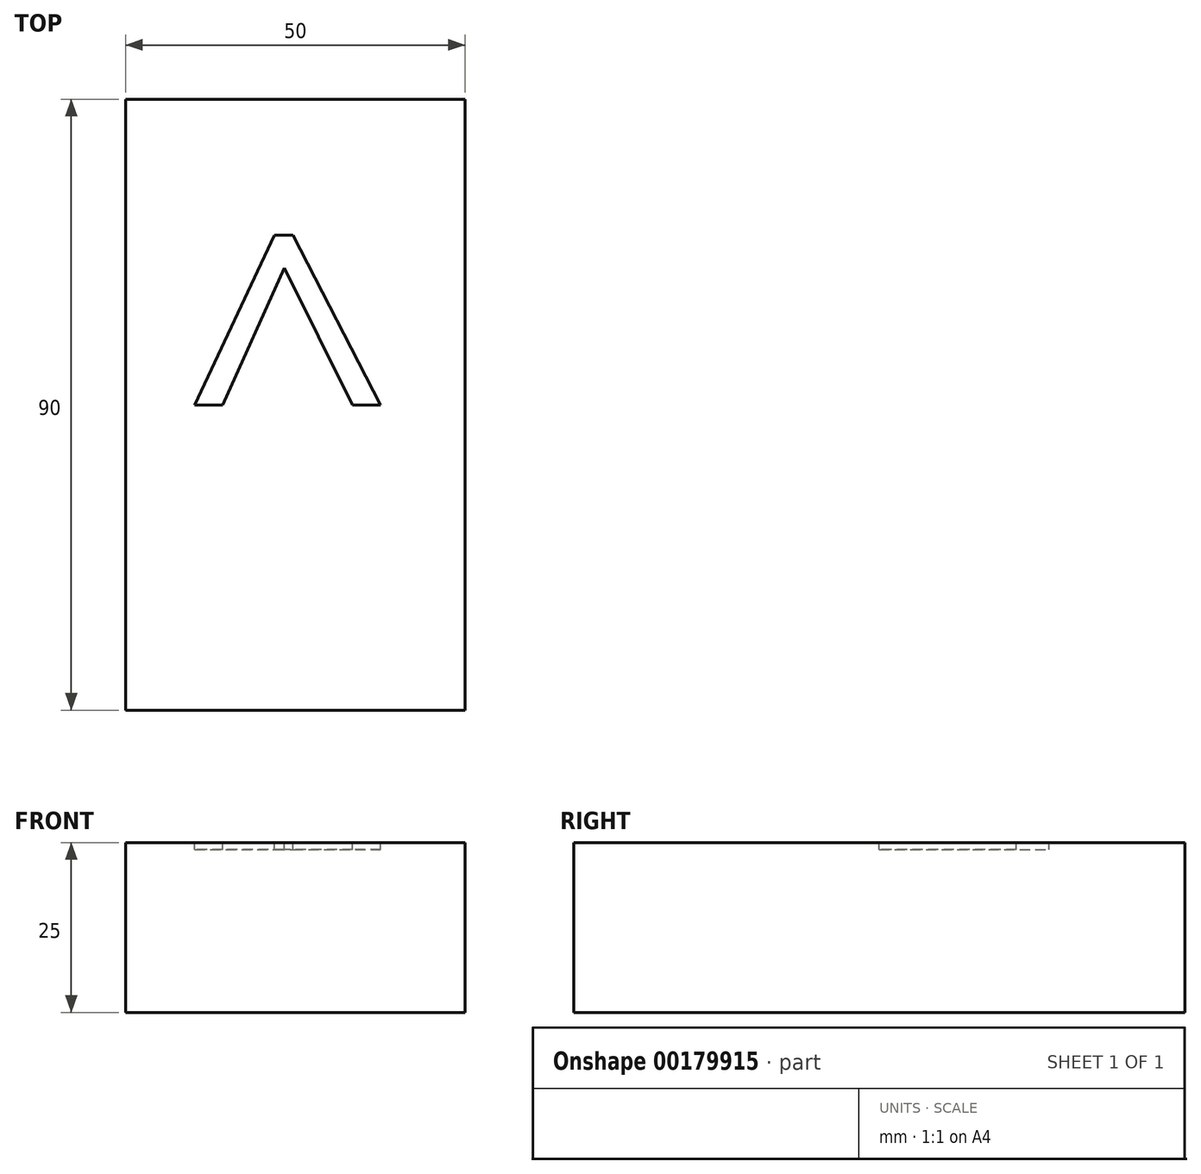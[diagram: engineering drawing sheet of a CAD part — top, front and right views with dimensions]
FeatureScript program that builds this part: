
annotation { "Feature Type Name" : "Feature", "Feature Type Description" : "" }
export const myFeature = defineFeature(function(context is Context, id is Id, definition is map)
    precondition{}
    {
        {
            var Q0;
            Q0=qCreatedBy(makeId("Top.planeOp"),FACE);
            var sketch = newSketch(context, id + "F0", { "sketchPlane" : qUnion([Q0])});
            skLineSegment(sketch, "E0.bottom", {"start": v(0, 0) * mm, "end": v(25, 0) * mm});
            skLineSegment(sketch, "E0.top", {"start": v(0, 90) * mm, "end": v(25, 90) * mm});
            skLineSegment(sketch, "E0.right", {"start": v(25, 0) * mm, "end": v(25, 90) * mm});
            skLineSegment(sketch, "E1.bottom", {"start": v(0, 0) * mm, "end": v(-25, 0) * mm});
            skLineSegment(sketch, "E1.top", {"start": v(0, 90) * mm, "end": v(-25, 90) * mm});
            skLineSegment(sketch, "E1.right", {"start": v(-25, 0) * mm, "end": v(-25, 90) * mm});
            skSolve(sketch);
        }
        {
            var Q0;
            Q0 = qSketchRegion(id + "F0", true);
            extrude(context, id + "F1", {"entities" : qUnion([Q0]), "depth" : 25 * mm});
        }
        {
            var Q0;
            Q0=makeQuery(id+"F1.opExtrude","CAP_FACE",FACE,{"disambiguationData":[OSD([sQuery(id+"F0.wireOp",EDGE,"E0.bottom"),sQuery(id+"F0.wireOp",EDGE,"E0.top"),sQuery(id+"F0.wireOp",EDGE,"E0.right"),sQuery(id+"F0.wireOp",EDGE,"E1.bottom"),sQuery(id+"F0.wireOp",EDGE,"E1.top"),sQuery(id+"F0.wireOp",EDGE,"E1.right")])],"isStart":false});
            var sketch = newSketch(context, id + "F2", { "sketchPlane" : qUnion([Q0])});
            skLineSegment(sketch, "E2", {"start": v(0, 90) * mm, "end": v(0, 67.59) * mm, "construction": true});
            skText(sketch, "E3", { "text": "^", "fontName": "OpenSans-Regular.ttf"});
            const initialGuessF2  = {"E3": [-0.01616, 0.03, 1, 0, 0.04]};
            skSetInitialGuess(sketch, initialGuessF2);
            skSolve(sketch);
        }
        {
            var Q0;
            Q0 = qSketchRegion(id + "F2", true);
            extrude(context, id + "F3", {"entities" : qUnion([Q0]), "operationType" : NewBodyOperationType.REMOVE, "oppositeDirection" : true, "depth" : 1 * mm});
        }
    });
